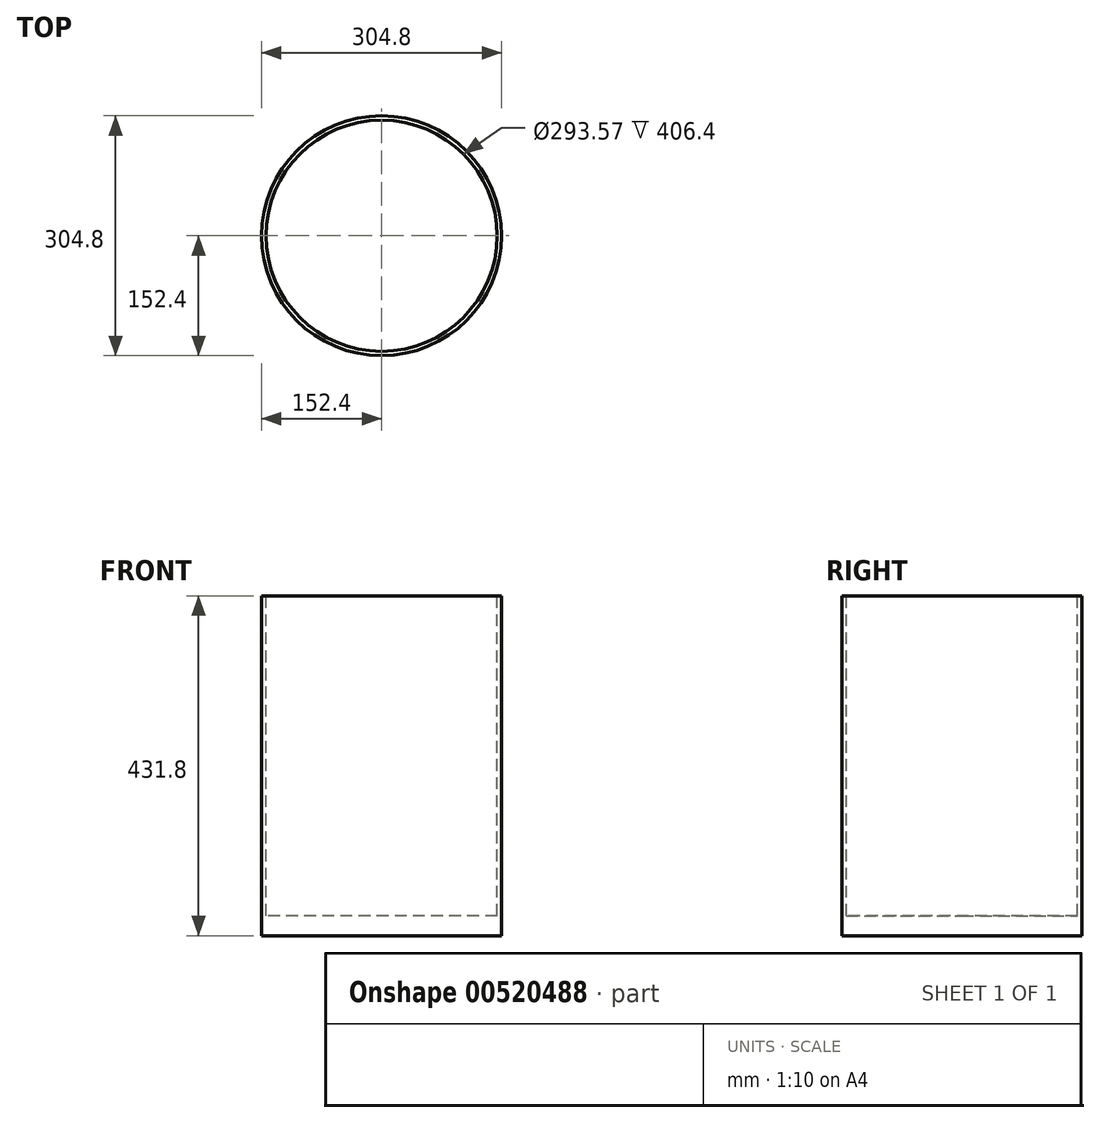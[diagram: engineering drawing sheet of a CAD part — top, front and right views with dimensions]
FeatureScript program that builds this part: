
annotation { "Feature Type Name" : "Feature", "Feature Type Description" : "" }
export const myFeature = defineFeature(function(context is Context, id is Id, definition is map)
    precondition{}
    {
        {
            var Q0;
            Q0=qCreatedBy(makeId("Top.planeOp"),FACE);
            var sketch = newSketch(context, id + "F0", { "sketchPlane" : qUnion([Q0])});
            skCircle(sketch, "E0", {"center": v(0, 0) * mm, "radius": 152.4 * mm});
            skSolve(sketch);
        }
        {
            var Q0;
            Q0 = qSketchRegion(id + "F0", true);
            extrude(context, id + "F1", {"entities" : qUnion([Q0]), "depth" : 431.8 * mm, "offsetDistance" : 25.4 * mm});
        }
        {
            var Q0;
            Q0=makeQuery(id+"F1.opExtrude","CAP_FACE",FACE,{"disambiguationData":[OSD([sQuery(id+"F0.wireOp",EDGE,"E0")])],"isStart":false});
            var sketch = newSketch(context, id + "F2", { "sketchPlane" : qUnion([Q0])});
            skLineSegment(sketch, "E1", {"start": v(22.04, 150.8) * mm, "end": v(0, 0) * mm});
            skCircle(sketch, "E2", {"center": v(0, 0) * mm, "radius": 146.79 * mm});
            skSolve(sketch);
        }
        {
            var Q0;
            Q0=makeQuery(id+"F2.imprint","IMPRINT",FACE,{"disambiguationData":[TD([[makeQuery(id+"F2.imprint","IMPRINT",EDGE,{"derivedFrom":sQuery(id+"F2.wireOp",EDGE,"E2")}),1.0]])]});
            extrude(context, id + "F3", {"entities" : qUnion([Q0]), "operationType" : NewBodyOperationType.REMOVE, "oppositeDirection" : true, "depth" : 406.4 * mm, "offsetDistance" : 25.4 * mm});
        }
    });
